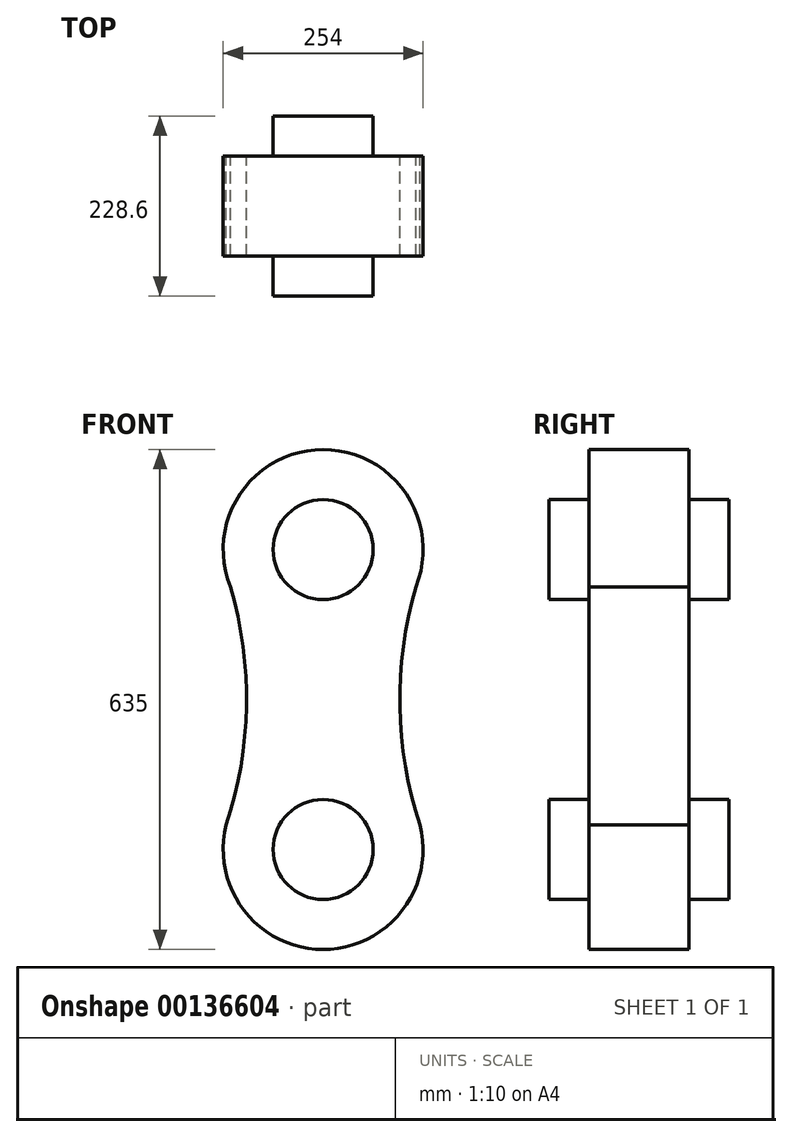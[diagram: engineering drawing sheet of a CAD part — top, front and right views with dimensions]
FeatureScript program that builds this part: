
annotation { "Feature Type Name" : "Feature", "Feature Type Description" : "" }
export const myFeature = defineFeature(function(context is Context, id is Id, definition is map)
    precondition{}
    {
        {
            var Q0;
            Q0=qCreatedBy(makeId("Front.planeOp"),FACE);
            var sketch = newSketch(context, id + "F0", { "sketchPlane" : qUnion([Q0])});
            skArc(sketch, "E0", {"start": v(117.73, 142.88) * mm, "mid": v(0, 317.5) * mm, "end": v(-117.73, 142.88) * mm});
            skArc(sketch, "E1", {"start": v(-118.68, -145.3) * mm, "mid": v(0, -317.5) * mm, "end": v(118.68, -145.3) * mm});
            skCircle(sketch, "E2", {"center": v(0, 190.5) * mm, "radius": 63.5 * mm});
            skCircle(sketch, "E3", {"center": v(0, -190.5) * mm, "radius": 63.5 * mm});
            skArc(sketch, "E4", {"start": v(-123.14, -159.44) * mm, "mid": v(-97.42, -8.7) * mm, "end": v(-117.73, 142.88) * mm});
            skArc(sketch, "E5.MirrorCS", {"start": v(123.14, -159.44) * mm, "mid": v(97.42, -8.7) * mm, "end": v(117.73, 142.88) * mm});
            skSolve(sketch);
        }
        {
            var Q0;
            {var subQ5=sQuery(id+"F0.wireOp",EDGE,"E0");Q0=makeQuery(id+"F0.imprint","IMPRINT",FACE,{"disambiguationData":[TD([[makeQuery(id+"F0.imprint","IMPRINT",EDGE,{"derivedFrom":subQ5}),1.0]])]});}
            extrude(context, id + "F1", {"entities" : qUnion([Q0]), "depth" : 127 * mm, "symmetric" : true});
        }
        {
            var Q0;
            Q0=qCreatedBy(makeId("Front.planeOp"),FACE);
            var sketch = newSketch(context, id + "F2", { "sketchPlane" : qUnion([Q0])});
            skCircle(sketch, "E6", {"center": v(0, 190.5) * mm, "radius": 63.5 * mm});
            skCircle(sketch, "E7", {"center": v(0, -190.5) * mm, "radius": 63.5 * mm});
            skSolve(sketch);
        }
        {
            var Q0;
            Q0 = qSketchRegion(id + "F2", true);
            extrude(context, id + "F3", {"entities" : qUnion([Q0]), "operationType" : NewBodyOperationType.ADD, "depth" : 228.6 * mm, "symmetric" : true});
        }
    });
